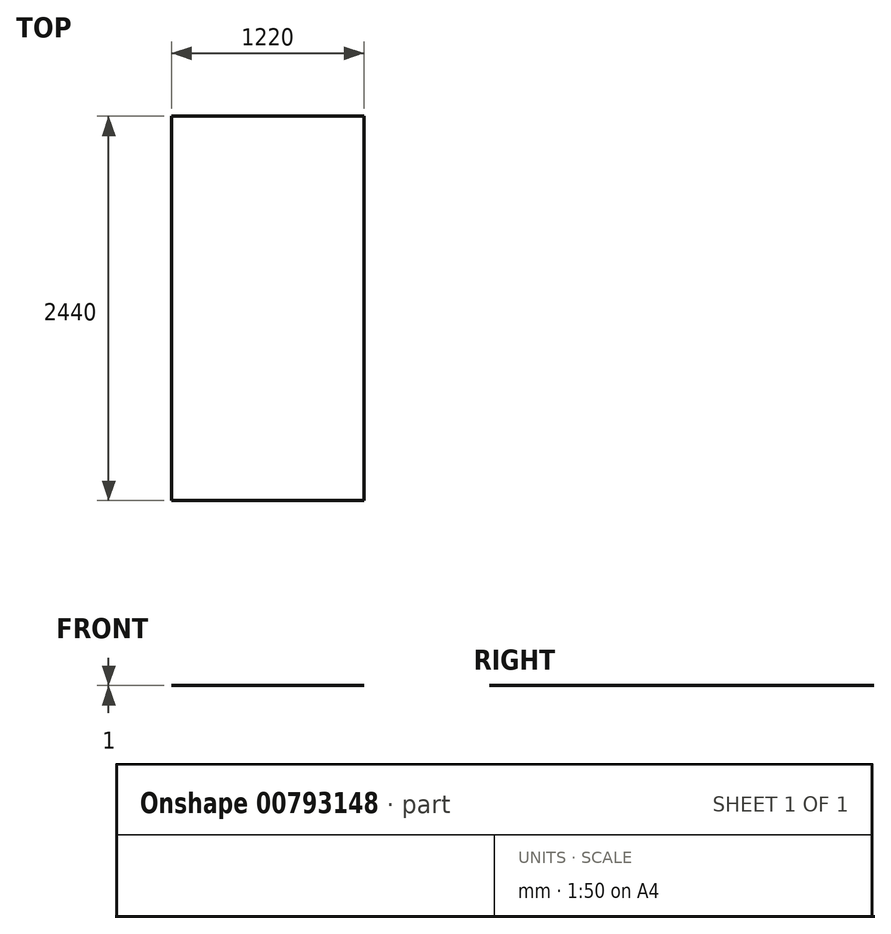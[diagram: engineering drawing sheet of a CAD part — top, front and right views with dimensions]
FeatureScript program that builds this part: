
annotation { "Feature Type Name" : "Feature", "Feature Type Description" : "" }
export const myFeature = defineFeature(function(context is Context, id is Id, definition is map)
    precondition{}
    {
        {
            var Q0;
            Q0=qCreatedBy(makeId("Top.planeOp"),FACE);
            var sketch = newSketch(context, id + "F0", { "sketchPlane" : qUnion([Q0])});
            skLineSegment(sketch, "E0.bottom", {"start": v(610, -1220) * mm, "end": v(-610, -1220) * mm});
            skLineSegment(sketch, "E0.top", {"start": v(610, 1220) * mm, "end": v(-610, 1220) * mm});
            skLineSegment(sketch, "E0.left", {"start": v(610, -1220) * mm, "end": v(610, 1220) * mm});
            skLineSegment(sketch, "E0.right", {"start": v(-610, -1220) * mm, "end": v(-610, 1220) * mm});
            skPoint(sketch, "E0.middle", {"position": v(0, 0) * mm});
            skSolve(sketch);
        }
        {
            var Q0;
            Q0=makeQuery(id+"F0.imprint","IMPRINT",FACE,{"disambiguationData":[TD([[makeQuery(id+"F0.imprint","IMPRINT",EDGE,{"derivedFrom":sQuery(id+"F0.wireOp",EDGE,"E0.bottom")}),-1.0]])]});
            extrude(context, id + "F1", {"entities" : qUnion([Q0]), "depth" : 1 * mm, "offsetDistance" : 25 * mm});
        }
    });
